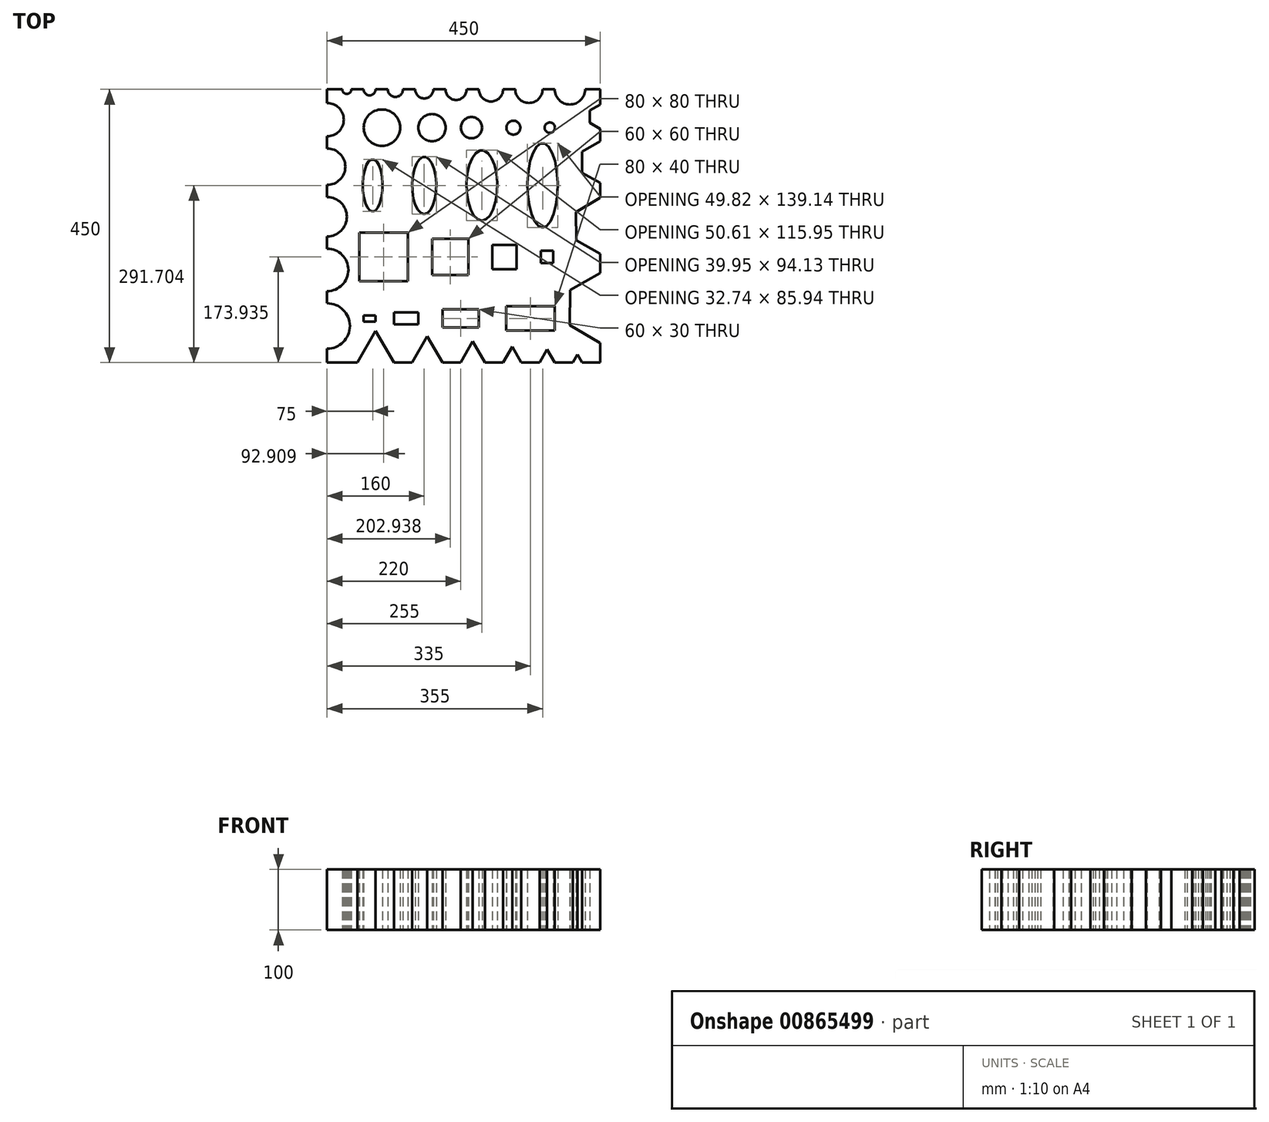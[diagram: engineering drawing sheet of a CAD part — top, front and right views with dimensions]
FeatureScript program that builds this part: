
annotation { "Feature Type Name" : "Feature", "Feature Type Description" : "" }
export const myFeature = defineFeature(function(context is Context, id is Id, definition is map)
    precondition{}
    {
        {
            var Q0;
            Q0=qCreatedBy(makeId("Top.planeOp"),FACE);
            var sketch = newSketch(context, id + "F0", { "sketchPlane" : qUnion([Q0])});
            skLineSegment(sketch, "E0.bottom", {"start": v(0, 0) * mm, "end": v(450, 0) * mm});
            skLineSegment(sketch, "E0.top", {"start": v(0, -450) * mm, "end": v(450, -450) * mm});
            skLineSegment(sketch, "E0.left", {"start": v(0, 0) * mm, "end": v(0, -450) * mm});
            skLineSegment(sketch, "E0.right", {"start": v(450, 0) * mm, "end": v(450, -450) * mm});
            skCircle(sketch, "E1", {"center": v(32.5, 0) * mm, "radius": 7.5 * mm});
            skCircle(sketch, "E2", {"center": v(70, 0) * mm, "radius": 10 * mm});
            skCircle(sketch, "E3", {"center": v(112.5, 0) * mm, "radius": 12.5 * mm});
            skCircle(sketch, "E4", {"center": v(212.5, 0) * mm, "radius": 17.5 * mm});
            skCircle(sketch, "E5", {"center": v(270, 0) * mm, "radius": 20 * mm});
            skPoint(sketch, "E6", {"position": v(0, -225) * mm});
            skCircle(sketch, "E7", {"center": v(160, 0) * mm, "radius": 15 * mm});
            skCircle(sketch, "E8", {"center": v(332.5, 0) * mm, "radius": 22.5 * mm});
            skCircle(sketch, "E9", {"center": v(400, 0) * mm, "radius": 25 * mm});
            skCircle(sketch, "E10", {"center": v(0, -50) * mm, "radius": 27.5 * mm});
            skCircle(sketch, "E11", {"center": v(0, -127.5) * mm, "radius": 30 * mm});
            skCircle(sketch, "E12", {"center": v(0, -210) * mm, "radius": 32.5 * mm});
            skCircle(sketch, "E13", {"center": v(0, -297.5) * mm, "radius": 35 * mm});
            skCircle(sketch, "E14", {"center": v(0, -390) * mm, "radius": 37.5 * mm});
            skCircle(sketch, "E15.cCircle", {"center": v(450, -45) * mm, "radius": 20 * mm, "construction": true});
            skLineSegment(sketch, "E15.0", {"start": v(450, -65) * mm, "end": v(432.68, -55) * mm});
            skLineSegment(sketch, "E15.1", {"start": v(432.68, -55) * mm, "end": v(432.68, -35) * mm});
            skLineSegment(sketch, "E15.2", {"start": v(432.68, -35) * mm, "end": v(450, -25) * mm});
            skLineSegment(sketch, "E15.3", {"start": v(450, -25) * mm, "end": v(467.32, -35) * mm});
            skLineSegment(sketch, "E15.4", {"start": v(467.32, -35) * mm, "end": v(467.32, -55) * mm});
            skLineSegment(sketch, "E15.5", {"start": v(467.32, -55) * mm, "end": v(450, -65) * mm});
            skCircle(sketch, "E16.cCircle", {"center": v(450, -120) * mm, "radius": 34.64 * mm, "construction": true});
            skLineSegment(sketch, "E16.0", {"start": v(420.17, -137.61) * mm, "end": v(419.83, -102.97) * mm});
            skLineSegment(sketch, "E16.1", {"start": v(419.83, -102.97) * mm, "end": v(449.66, -85.36) * mm});
            skLineSegment(sketch, "E16.2", {"start": v(449.66, -85.36) * mm, "end": v(479.83, -102.39) * mm});
            skLineSegment(sketch, "E16.3", {"start": v(479.83, -102.39) * mm, "end": v(480.17, -137.03) * mm});
            skLineSegment(sketch, "E16.4", {"start": v(480.17, -137.03) * mm, "end": v(450.34, -154.64) * mm});
            skLineSegment(sketch, "E16.5", {"start": v(450.34, -154.64) * mm, "end": v(420.17, -137.61) * mm});
            skCircle(sketch, "E17.cCircle", {"center": v(450, -225) * mm, "radius": 46.19 * mm, "construction": true});
            skLineSegment(sketch, "E17.0", {"start": v(410.35, -248.7) * mm, "end": v(409.66, -202.51) * mm});
            skLineSegment(sketch, "E17.1", {"start": v(409.66, -202.51) * mm, "end": v(449.3, -178.82) * mm});
            skLineSegment(sketch, "E17.2", {"start": v(449.3, -178.82) * mm, "end": v(489.65, -201.3) * mm});
            skLineSegment(sketch, "E17.3", {"start": v(489.65, -201.3) * mm, "end": v(490.34, -247.49) * mm});
            skLineSegment(sketch, "E17.4", {"start": v(490.34, -247.49) * mm, "end": v(450.7, -271.18) * mm});
            skLineSegment(sketch, "E17.5", {"start": v(450.7, -271.18) * mm, "end": v(410.35, -248.7) * mm});
            skCircle(sketch, "E18.cCircle", {"center": v(450, -360) * mm, "radius": 57.74 * mm, "construction": true});
            skLineSegment(sketch, "E18.0", {"start": v(400.24, -330.72) * mm, "end": v(450.48, -302.27) * mm});
            skLineSegment(sketch, "E18.1", {"start": v(450.48, -302.27) * mm, "end": v(500.24, -331.55) * mm});
            skLineSegment(sketch, "E18.2", {"start": v(500.24, -331.55) * mm, "end": v(499.76, -389.28) * mm});
            skLineSegment(sketch, "E18.3", {"start": v(499.76, -389.28) * mm, "end": v(449.52, -417.73) * mm});
            skLineSegment(sketch, "E18.4", {"start": v(449.52, -417.73) * mm, "end": v(399.76, -388.45) * mm});
            skLineSegment(sketch, "E18.5", {"start": v(399.76, -388.45) * mm, "end": v(400.24, -330.72) * mm});
            skLineSegment(sketch, "E19", {"start": v(420, -450) * mm, "end": v(412.5, -437) * mm});
            skLineSegment(sketch, "E20", {"start": v(412.5, -437) * mm, "end": v(405, -450) * mm});
            skLineSegment(sketch, "E21", {"start": v(420, -450) * mm, "end": v(405, -450) * mm});
            skLineSegment(sketch, "E22", {"start": v(375, -450) * mm, "end": v(362.5, -428.35) * mm});
            skLineSegment(sketch, "E23", {"start": v(362.5, -428.35) * mm, "end": v(350, -450) * mm});
            skLineSegment(sketch, "E24", {"start": v(350, -450) * mm, "end": v(375, -450) * mm});
            skLineSegment(sketch, "E25", {"start": v(320, -450) * mm, "end": v(305, -424.02) * mm});
            skLineSegment(sketch, "E26", {"start": v(305, -424.02) * mm, "end": v(290, -450) * mm});
            skLineSegment(sketch, "E27", {"start": v(290, -450) * mm, "end": v(320, -450) * mm});
            skLineSegment(sketch, "E28", {"start": v(260, -450) * mm, "end": v(220, -450) * mm});
            skLineSegment(sketch, "E29", {"start": v(220, -450) * mm, "end": v(240, -415.36) * mm});
            skLineSegment(sketch, "E30", {"start": v(240, -415.36) * mm, "end": v(260, -450) * mm});
            skLineSegment(sketch, "E31", {"start": v(190, -450) * mm, "end": v(140, -450) * mm});
            skLineSegment(sketch, "E32", {"start": v(140, -450) * mm, "end": v(165, -406.7) * mm});
            skLineSegment(sketch, "E33", {"start": v(165, -406.7) * mm, "end": v(190, -450) * mm});
            skLineSegment(sketch, "E34", {"start": v(110, -450) * mm, "end": v(50, -450) * mm});
            skLineSegment(sketch, "E35", {"start": v(50, -450) * mm, "end": v(80, -398.04) * mm});
            skLineSegment(sketch, "E36", {"start": v(80, -398.04) * mm, "end": v(110, -450) * mm});
            skCircle(sketch, "E37", {"center": v(366.86, -63.19) * mm, "radius": 8.5 * mm});
            skCircle(sketch, "E38", {"center": v(306.86, -63.19) * mm, "radius": 11.5 * mm});
            skCircle(sketch, "E39", {"center": v(237.86, -63.19) * mm, "radius": 17.5 * mm});
            skCircle(sketch, "E40", {"center": v(172.86, -63.19) * mm, "radius": 22.5 * mm});
            skCircle(sketch, "E41", {"center": v(90.36, -63.19) * mm, "radius": 30 * mm});
            skPoint(sketch, "E42.cornerSnap0", {"position": v(400, -359.59) * mm});
            skEllipse(sketch, "E43", {"center": v(355, -158.3) * mm, "majorRadius": 69.57 * mm, "minorRadius": 24.91 * mm, "majorAxis": v(0, -1)});
            skEllipse(sketch, "E44", {"center": v(255, -158.3) * mm, "majorRadius": 57.98 * mm, "minorRadius": 25.3 * mm, "majorAxis": v(0, -1)});
            skEllipse(sketch, "E45", {"center": v(160, -158.3) * mm, "majorRadius": 47.06 * mm, "minorRadius": 19.98 * mm, "majorAxis": v(0, -1)});
            skEllipse(sketch, "E46", {"center": v(75, -158.3) * mm, "majorRadius": 42.97 * mm, "minorRadius": 16.37 * mm, "majorAxis": v(0, -1)});
            skLineSegment(sketch, "E47.bottom", {"start": v(132.9, -316.06) * mm, "end": v(52.9, -316.06) * mm});
            skLineSegment(sketch, "E47.top", {"start": v(132.9, -236.06) * mm, "end": v(52.9, -236.06) * mm});
            skLineSegment(sketch, "E47.left", {"start": v(132.9, -316.06) * mm, "end": v(132.9, -236.06) * mm});
            skLineSegment(sketch, "E47.right", {"start": v(52.9, -316.06) * mm, "end": v(52.9, -236.06) * mm});
            skPoint(sketch, "E47.middle", {"position": v(92.9, -276.06) * mm});
            skLineSegment(sketch, "E48.bottom", {"start": v(232.94, -306.06) * mm, "end": v(172.94, -306.06) * mm});
            skLineSegment(sketch, "E48.top", {"start": v(232.94, -246.06) * mm, "end": v(172.94, -246.06) * mm});
            skLineSegment(sketch, "E48.left", {"start": v(232.94, -306.06) * mm, "end": v(232.94, -246.06) * mm});
            skLineSegment(sketch, "E48.right", {"start": v(172.94, -306.06) * mm, "end": v(172.94, -246.06) * mm});
            skPoint(sketch, "E48.middle", {"position": v(202.94, -276.06) * mm});
            skLineSegment(sketch, "E49.bottom", {"start": v(312.28, -296.06) * mm, "end": v(272.28, -296.06) * mm});
            skLineSegment(sketch, "E49.top", {"start": v(312.28, -256.06) * mm, "end": v(272.28, -256.06) * mm});
            skLineSegment(sketch, "E49.left", {"start": v(312.28, -296.06) * mm, "end": v(312.28, -256.06) * mm});
            skLineSegment(sketch, "E49.right", {"start": v(272.28, -296.06) * mm, "end": v(272.28, -256.06) * mm});
            skPoint(sketch, "E49.middle", {"position": v(292.28, -276.06) * mm});
            skLineSegment(sketch, "E50.bottom", {"start": v(372.3, -286.06) * mm, "end": v(352.3, -286.06) * mm});
            skLineSegment(sketch, "E50.top", {"start": v(372.3, -266.06) * mm, "end": v(352.3, -266.06) * mm});
            skLineSegment(sketch, "E50.left", {"start": v(372.3, -286.06) * mm, "end": v(372.3, -266.06) * mm});
            skLineSegment(sketch, "E50.right", {"start": v(352.3, -286.06) * mm, "end": v(352.3, -266.06) * mm});
            skPoint(sketch, "E50.middle", {"position": v(362.3, -276.06) * mm});
            skLineSegment(sketch, "E51.bottom", {"start": v(80, -382.47) * mm, "end": v(60, -382.47) * mm});
            skLineSegment(sketch, "E51.top", {"start": v(80, -372.47) * mm, "end": v(60, -372.47) * mm});
            skLineSegment(sketch, "E51.left", {"start": v(80, -382.47) * mm, "end": v(80, -372.47) * mm});
            skLineSegment(sketch, "E51.right", {"start": v(60, -382.47) * mm, "end": v(60, -372.47) * mm});
            skPoint(sketch, "E51.middle", {"position": v(70, -377.47) * mm});
            skLineSegment(sketch, "E52.bottom", {"start": v(110, -387.47) * mm, "end": v(150, -387.47) * mm});
            skLineSegment(sketch, "E52.top", {"start": v(110, -367.47) * mm, "end": v(150, -367.47) * mm});
            skLineSegment(sketch, "E52.left", {"start": v(110, -387.47) * mm, "end": v(110, -367.47) * mm});
            skLineSegment(sketch, "E52.right", {"start": v(150, -387.47) * mm, "end": v(150, -367.47) * mm});
            skPoint(sketch, "E52.middle", {"position": v(130, -377.47) * mm});
            skLineSegment(sketch, "E53.bottom", {"start": v(190, -392.47) * mm, "end": v(250, -392.47) * mm});
            skLineSegment(sketch, "E53.top", {"start": v(190, -362.47) * mm, "end": v(250, -362.47) * mm});
            skLineSegment(sketch, "E53.left", {"start": v(190, -392.47) * mm, "end": v(190, -362.47) * mm});
            skLineSegment(sketch, "E53.right", {"start": v(250, -392.47) * mm, "end": v(250, -362.47) * mm});
            skPoint(sketch, "E53.middle", {"position": v(220, -377.47) * mm});
            skLineSegment(sketch, "E54.bottom", {"start": v(375, -397.47) * mm, "end": v(295, -397.47) * mm});
            skLineSegment(sketch, "E54.top", {"start": v(375, -357.47) * mm, "end": v(295, -357.47) * mm});
            skLineSegment(sketch, "E54.left", {"start": v(375, -397.47) * mm, "end": v(375, -357.47) * mm});
            skLineSegment(sketch, "E54.right", {"start": v(295, -397.47) * mm, "end": v(295, -357.47) * mm});
            skPoint(sketch, "E54.middle", {"position": v(335, -377.47) * mm});
            skLineSegment(sketch, "E55", {"start": v(0, 0) * mm, "end": v(-63.64, 63.64) * mm});
            skLineSegment(sketch, "E56", {"start": v(-63.64, 63.64) * mm, "end": v(513.64, 63.64) * mm});
            skLineSegment(sketch, "E57", {"start": v(513.64, 63.64) * mm, "end": v(450, 0) * mm});
            skLineSegment(sketch, "E58", {"start": v(513.64, 63.64) * mm, "end": v(513.64, -513.64) * mm});
            skLineSegment(sketch, "E59", {"start": v(513.64, -513.64) * mm, "end": v(450, -450) * mm});
            skLineSegment(sketch, "E60", {"start": v(-63.64, 63.64) * mm, "end": v(-63.64, -513.64) * mm});
            skLineSegment(sketch, "E61", {"start": v(-63.64, -513.64) * mm, "end": v(0, -450) * mm});
            skLineSegment(sketch, "E62", {"start": v(-63.64, -513.64) * mm, "end": v(513.64, -513.64) * mm});
            skSolve(sketch);
        }
        {
            var Q0;
            {var subQ70=sQuery(id+"F0.wireOp",EDGE,"E15.0");Q0=makeQuery(id+"F0.imprint","IMPRINT",FACE,{"disambiguationData":[TD([[makeQuery(id+"F0.imprint","IMPRINT",EDGE,{"derivedFrom":subQ70}),1.0]])]});}
            extrude(context, id + "F1", {"entities" : qUnion([Q0]), "depth" : 100 * mm, "offsetDistance" : 25 * mm});
        }
    });
